# Revit family: 201_RIX-_
name_source: partatom
category: Air Terminals
units: mm (PartAtom-declared; Revit-internal decimal feet)

## family parameters
Always vertical = Yes
Cut with Voids When Loaded = No
Part Type = Normal
Room Calculation Point = Yes
Round Connector Dimension = Use Diameter
Shared = No
Work Plane-Based = No

## types (3) — shared parameters
CAT0 = Yes
CL_Location_5000 = 5000 mm  [stored 16.4042 ft]
Description = Supply air device
L_ARR = 400 mm  [stored 1.31234 ft]
Manufacturer = Climecon
QmdConnectorList = 201;D
URL = www.climecon.fi
W_ARR = 400 mm  [stored 1.31234 ft]
magiPartTypeId = 201
magiProductFamilyId = RIX-*
zero-valued in all types: CLBTZ, H_ARR

## per-type parameters (varying)
| type | A | D | E | E__ve |
| RIX-250 | 256 mm | 248 mm | 320 mm | -320 mm  [stored -1.04987 ft] |
| RIX-315 | 321 mm | 313 mm | 390 mm | -390 mm |
| RIX-400 | 406 mm  [stored 1.33202 ft] | 398 mm | 480 mm  [stored 1.5748 ft] | -480 mm  [stored -1.5748 ft] |

note: column(s) folded — value = type name in every type: MC Product Code, magiProductId

note: [stored X ft] marks values corroborated as IEEE doubles in the binary element streams (Revit-internal decimal feet)

## geometry (parser evidence)
native form markers: Sweep x1
no freeform markers — native parametric forms only
